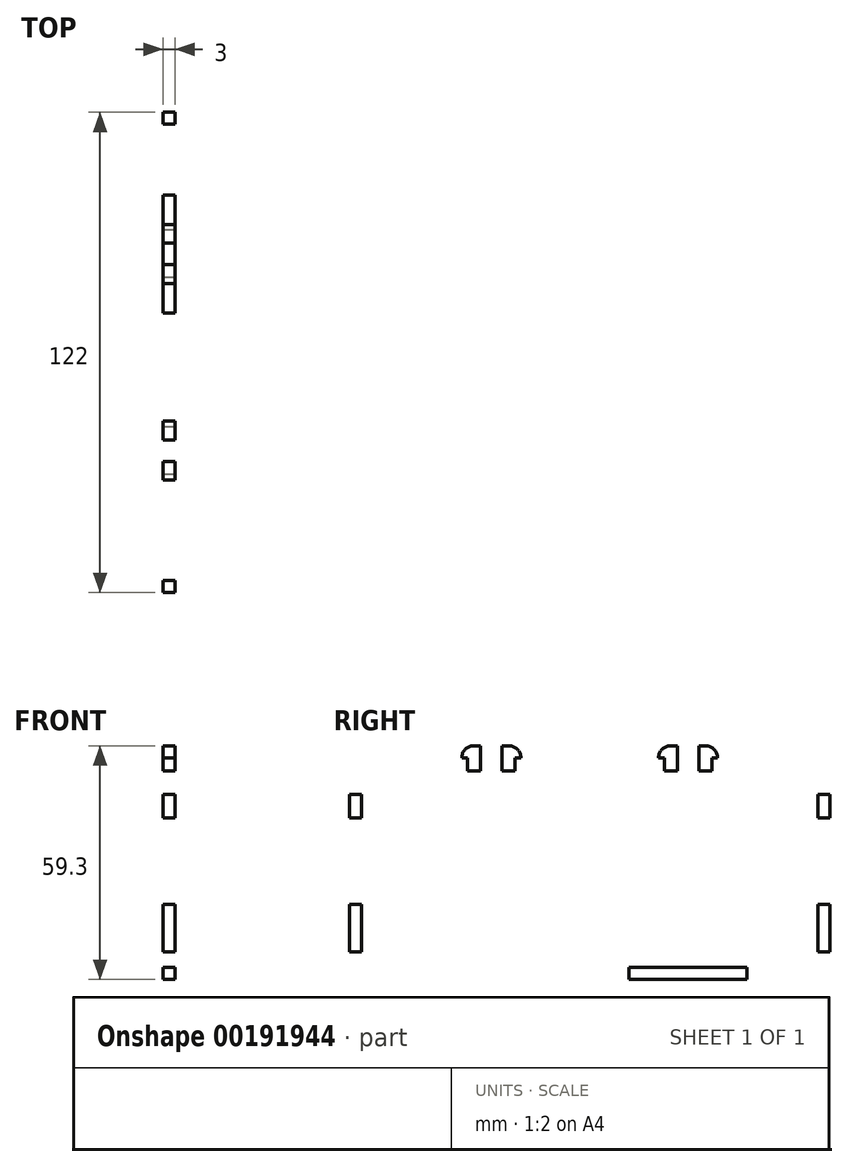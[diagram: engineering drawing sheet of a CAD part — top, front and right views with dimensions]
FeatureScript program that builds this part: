
annotation { "Feature Type Name" : "Feature", "Feature Type Description" : "" }
export const myFeature = defineFeature(function(context is Context, id is Id, definition is map)
    precondition{}
    {
        {
            var Q0;
            Q0=qCreatedBy(makeId("Right.planeOp"),FACE);
            var sketch = newSketch(context, id + "F0", { "sketchPlane" : qUnion([Q0])});
            skLineSegment(sketch, "E0.bottom", {"start": v(58, -25) * mm, "end": v(-58, -25) * mm});
            skLineSegment(sketch, "E0.top", {"start": v(58, 25) * mm, "end": v(-58, 25) * mm});
            skLineSegment(sketch, "E0.left", {"start": v(58, -25) * mm, "end": v(58, 25) * mm});
            skLineSegment(sketch, "E0.right", {"start": v(-58, -25) * mm, "end": v(-58, 25) * mm});
            skPoint(sketch, "E0.middle", {"position": v(0, 0) * mm});
            skLineSegment(sketch, "E1.bottom", {"start": v(-10, -25) * mm, "end": v(-40, -25) * mm});
            skLineSegment(sketch, "E1.top", {"start": v(-10, -28) * mm, "end": v(-40, -28) * mm});
            skLineSegment(sketch, "E1.left", {"start": v(-10, -25) * mm, "end": v(-10, -28) * mm});
            skLineSegment(sketch, "E1.right", {"start": v(-40, -25) * mm, "end": v(-40, -28) * mm});
            skLineSegment(sketch, "E2.bottom", {"start": v(-50.3, -25) * mm, "end": v(-47, -25) * mm});
            skLineSegment(sketch, "E2.top", {"start": v(-50.3, -17) * mm, "end": v(-47, -17) * mm});
            skLineSegment(sketch, "E2.left", {"start": v(-50.3, -25) * mm, "end": v(-50.3, -17) * mm});
            skLineSegment(sketch, "E2.right", {"start": v(-47, -25) * mm, "end": v(-47, -17) * mm});
            skPoint(sketch, "E3", {"position": v(-48.65, -25) * mm});
            skLineSegment(sketch, "E4.bottom", {"start": v(-45.15, -21) * mm, "end": v(-52.15, -21) * mm});
            skLineSegment(sketch, "E4.top", {"start": v(-45.15, -19) * mm, "end": v(-52.15, -19) * mm});
            skLineSegment(sketch, "E4.left", {"start": v(-45.15, -21) * mm, "end": v(-45.15, -19) * mm});
            skLineSegment(sketch, "E4.right", {"start": v(-52.15, -21) * mm, "end": v(-52.15, -19) * mm});
            skPoint(sketch, "E4.middle", {"position": v(-48.65, -20) * mm});
            skCircle(sketch, "E5", {"center": v(-52.15, -21) * mm, "radius": 0.5 * mm});
            skCircle(sketch, "E6", {"center": v(-45.15, -21) * mm, "radius": 0.5 * mm});
            skPoint(sketch, "E7", {"position": v(-58, 0) * mm});
            skLineSegment(sketch, "E8.bottom", {"start": v(-58, -1.65) * mm, "end": v(-50, -1.65) * mm});
            skLineSegment(sketch, "E8.top", {"start": v(-58, 1.65) * mm, "end": v(-50, 1.65) * mm});
            skLineSegment(sketch, "E8.left", {"start": v(-58, -1.65) * mm, "end": v(-58, 1.65) * mm});
            skLineSegment(sketch, "E8.right", {"start": v(-50, -1.65) * mm, "end": v(-50, 1.65) * mm});
            skPoint(sketch, "E8.middle", {"position": v(-54, 0) * mm});
            skLineSegment(sketch, "E9.bottom", {"start": v(-52, -3.5) * mm, "end": v(-54, -3.5) * mm});
            skLineSegment(sketch, "E9.top", {"start": v(-52, 3.5) * mm, "end": v(-54, 3.5) * mm});
            skLineSegment(sketch, "E9.left", {"start": v(-52, -3.5) * mm, "end": v(-52, 3.5) * mm});
            skLineSegment(sketch, "E9.right", {"start": v(-54, -3.5) * mm, "end": v(-54, 3.5) * mm});
            skPoint(sketch, "E9.middle", {"position": v(-53, 0) * mm});
            skCircle(sketch, "E10", {"center": v(-54, 3.5) * mm, "radius": 0.5 * mm});
            skCircle(sketch, "E11", {"center": v(-54, -3.5) * mm, "radius": 0.5 * mm});
            skLineSegment(sketch, "E12.bottom", {"start": v(-58, -21) * mm, "end": v(-61, -21) * mm});
            skLineSegment(sketch, "E12.top", {"start": v(-58, -9) * mm, "end": v(-61, -9) * mm});
            skLineSegment(sketch, "E12.left", {"start": v(-58, -21) * mm, "end": v(-58, -9) * mm});
            skLineSegment(sketch, "E12.right", {"start": v(-61, -21) * mm, "end": v(-61, -9) * mm});
            skLineSegment(sketch, "E13.bottom", {"start": v(-58, 19) * mm, "end": v(-61, 19) * mm});
            skLineSegment(sketch, "E13.top", {"start": v(-58, 13) * mm, "end": v(-61, 13) * mm});
            skLineSegment(sketch, "E13.left", {"start": v(-58, 19) * mm, "end": v(-58, 13) * mm});
            skLineSegment(sketch, "E13.right", {"start": v(-61, 19) * mm, "end": v(-61, 13) * mm});
            skCircle(sketch, "E14.MirrorC", {"center": v(54, -3.5) * mm, "radius": 0.5 * mm});
            skCircle(sketch, "E15.MirrorC", {"center": v(54, 3.5) * mm, "radius": 0.5 * mm});
            skLineSegment(sketch, "E16.MirrorCS", {"start": v(58, 1.65) * mm, "end": v(50, 1.65) * mm});
            skLineSegment(sketch, "E17.MirrorCS", {"start": v(52, -3.5) * mm, "end": v(54, -3.5) * mm});
            skCircle(sketch, "E18.MirrorC", {"center": v(45.15, -21) * mm, "radius": 0.5 * mm});
            skLineSegment(sketch, "E19.MirrorCS", {"start": v(52.15, -21) * mm, "end": v(52.15, -19) * mm});
            skCircle(sketch, "E20.MirrorC", {"center": v(52.15, -21) * mm, "radius": 0.5 * mm});
            skLineSegment(sketch, "E21.MirrorCS", {"start": v(52, 3.5) * mm, "end": v(54, 3.5) * mm});
            skLineSegment(sketch, "E22.MirrorCS", {"start": v(45.15, -19) * mm, "end": v(52.15, -19) * mm});
            skLineSegment(sketch, "E23.MirrorCS", {"start": v(58, -1.65) * mm, "end": v(50, -1.65) * mm});
            skLineSegment(sketch, "E24.MirrorCS", {"start": v(58, 13) * mm, "end": v(61, 13) * mm});
            skLineSegment(sketch, "E25.MirrorCS", {"start": v(50, -1.65) * mm, "end": v(50, 1.65) * mm});
            skLineSegment(sketch, "E26.MirrorCS", {"start": v(52, -3.5) * mm, "end": v(52, 3.5) * mm});
            skLineSegment(sketch, "E27.MirrorCS", {"start": v(58, -21) * mm, "end": v(61, -21) * mm});
            skLineSegment(sketch, "E28.MirrorCS", {"start": v(45.15, -21) * mm, "end": v(45.15, -19) * mm});
            skLineSegment(sketch, "E29.MirrorCS", {"start": v(10, -25) * mm, "end": v(10, -28) * mm});
            skLineSegment(sketch, "E30.MirrorCS", {"start": v(58, 19) * mm, "end": v(61, 19) * mm});
            skLineSegment(sketch, "E31.MirrorCS", {"start": v(47, -25) * mm, "end": v(47, -17) * mm});
            skLineSegment(sketch, "E32.MirrorCS", {"start": v(50.3, -25) * mm, "end": v(47, -25) * mm});
            skLineSegment(sketch, "E33.MirrorCS", {"start": v(40, -25) * mm, "end": v(40, -28) * mm});
            skLineSegment(sketch, "E34.MirrorCS", {"start": v(58, -9) * mm, "end": v(61, -9) * mm});
            skLineSegment(sketch, "E35.MirrorCS", {"start": v(50.3, -25) * mm, "end": v(50.3, -17) * mm});
            skLineSegment(sketch, "E36.MirrorCS", {"start": v(58, -1.65) * mm, "end": v(58, 1.65) * mm});
            skLineSegment(sketch, "E37.MirrorCS", {"start": v(50.3, -17) * mm, "end": v(47, -17) * mm});
            skLineSegment(sketch, "E38.MirrorCS", {"start": v(54, -3.5) * mm, "end": v(54, 3.5) * mm});
            skLineSegment(sketch, "E39.MirrorCS", {"start": v(45.15, -21) * mm, "end": v(52.15, -21) * mm});
            skLineSegment(sketch, "E40.MirrorCS", {"start": v(61, 19) * mm, "end": v(61, 13) * mm});
            skLineSegment(sketch, "E41.MirrorCS", {"start": v(58, 19) * mm, "end": v(58, 13) * mm});
            skLineSegment(sketch, "E42.MirrorCS", {"start": v(61, -21) * mm, "end": v(61, -9) * mm});
            skPoint(sketch, "E43.MirrorP", {"position": v(48.65, -20) * mm});
            skPoint(sketch, "E44.MirrorP", {"position": v(54, 0) * mm});
            skLineSegment(sketch, "E45.MirrorCS", {"start": v(58, -21) * mm, "end": v(58, -9) * mm});
            skLineSegment(sketch, "E46.MirrorCS", {"start": v(10, -28) * mm, "end": v(40, -28) * mm});
            skLineSegment(sketch, "E47.MirrorCS", {"start": v(10, -25) * mm, "end": v(40, -25) * mm});
            skPoint(sketch, "E48.MirrorP", {"position": v(48.65, -25) * mm});
            skPoint(sketch, "E49.MirrorP", {"position": v(53, 0) * mm});
            skPoint(sketch, "E50.MirrorP", {"position": v(58, 0) * mm});
            skPoint(sketch, "E51", {"position": v(-31, 25) * mm});
            skPoint(sketch, "E52", {"position": v(-27.7, 25) * mm});
            skPoint(sketch, "E53", {"position": v(-34, 25) * mm});
            skPoint(sketch, "E54", {"position": v(-34, 15) * mm});
            skPoint(sketch, "E55", {"position": v(-31, 15) * mm});
            skPoint(sketch, "E56", {"position": v(-27.7, 15) * mm});
            skPoint(sketch, "E57", {"position": v(-34.3, 5) * mm});
            skPoint(sketch, "E58", {"position": v(-31, 5) * mm});
            skPoint(sketch, "E59", {"position": v(-37.3, 5) * mm});
            skLineSegment(sketch, "E60", {"start": v(-34, 25) * mm, "end": v(-34, 19.82) * mm});
            skLineSegment(sketch, "E61", {"start": v(-35.51, 10.42) * mm, "end": v(-35.79, 9.58) * mm});
            skLineSegment(sketch, "E62", {"start": v(-31, 25) * mm, "end": v(-31, 19.82) * mm});
            skLineSegment(sketch, "E63", {"start": v(-32.79, 9.58) * mm, "end": v(-32.51, 10.42) * mm});
            skLineSegment(sketch, "E64", {"start": v(-27.7, 25) * mm, "end": v(-27.7, 19.82) * mm});
            skLineSegment(sketch, "E65", {"start": v(-29.49, 9.58) * mm, "end": v(-29.21, 10.42) * mm});
            skPoint(sketch, "E66", {"position": v(-37.3, -5) * mm});
            skPoint(sketch, "E67", {"position": v(-34.3, -5) * mm});
            skPoint(sketch, "E68", {"position": v(-31, -5) * mm});
            skLineSegment(sketch, "E69", {"start": v(-37.3, 0.18) * mm, "end": v(-37.3, -5) * mm});
            skLineSegment(sketch, "E70", {"start": v(-34.3, 0.18) * mm, "end": v(-34.3, -5) * mm});
            skLineSegment(sketch, "E71", {"start": v(-31, 0.18) * mm, "end": v(-31, -5) * mm});
            skArc(sketch, "E72", {"start": v(-37.3, -5) * mm, "mid": v(-35.8, -6.5) * mm, "end": v(-34.3, -5) * mm});
            skArc(sketch, "E73", {"start": v(-31, -5) * mm, "mid": v(-25, -11) * mm, "end": v(-19, -5) * mm});
            skArc(sketch, "E74.filletArc", {"start": v(-35.51, 10.42) * mm, "mid": v(-34.38, 15.06) * mm, "end": v(-34, 19.82) * mm});
            skArc(sketch, "E75.filletArc", {"start": v(-35.79, 9.58) * mm, "mid": v(-36.92, 4.94) * mm, "end": v(-37.3, 0.18) * mm});
            skArc(sketch, "E76.filletArc", {"start": v(-32.51, 10.42) * mm, "mid": v(-31.38, 15.06) * mm, "end": v(-31, 19.82) * mm});
            skArc(sketch, "E77.filletArc", {"start": v(-32.79, 9.58) * mm, "mid": v(-33.92, 4.94) * mm, "end": v(-34.3, 0.18) * mm});
            skArc(sketch, "E78.filletArc", {"start": v(-29.21, 10.42) * mm, "mid": v(-28.08, 15.06) * mm, "end": v(-27.7, 19.82) * mm});
            skArc(sketch, "E79.filletArc", {"start": v(-29.49, 9.58) * mm, "mid": v(-30.62, 4.94) * mm, "end": v(-31, 0.18) * mm});
            skLineSegment(sketch, "E80", {"start": v(-31, 25) * mm, "end": v(-31, 28.3) * mm});
            skLineSegment(sketch, "E81", {"start": v(-31, 28.3) * mm, "end": v(-32.5, 28.3) * mm});
            skLineSegment(sketch, "E82", {"start": v(-32.5, 28.3) * mm, "end": v(-32.5, 28.3) * mm});
            skLineSegment(sketch, "E83", {"start": v(-29.5, 31.3) * mm, "end": v(-27.7, 31.3) * mm});
            skLineSegment(sketch, "E84", {"start": v(-27.7, 31.3) * mm, "end": v(-27.7, 25) * mm});
            skPoint(sketch, "E85.visualSharp", {"position": v(-32.5, 31.3) * mm});
            skArc(sketch, "E85.filletArc", {"start": v(-29.5, 31.3) * mm, "mid": v(-31.62, 30.42) * mm, "end": v(-32.5, 28.3) * mm});
            skPoint(sketch, "E86", {"position": v(-25, 25) * mm});
            skLineSegment(sketch, "E87", {"start": v(-25, 25) * mm, "end": v(-25, -5) * mm});
            skPoint(sketch, "E88.MirrorP", {"position": v(-22.3, 15) * mm});
            skLineSegment(sketch, "E89.MirrorCS", {"start": v(-20.5, 31.3) * mm, "end": v(-22.3, 31.3) * mm});
            skLineSegment(sketch, "E90.MirrorCS", {"start": v(-22.3, 31.3) * mm, "end": v(-22.3, 25) * mm});
            skLineSegment(sketch, "E91.MirrorCS", {"start": v(-22.3, 25) * mm, "end": v(-22.3, 19.82) * mm});
            skArc(sketch, "E92.MirrorCS", {"start": v(-20.79, 10.42) * mm, "mid": v(-21.92, 15.06) * mm, "end": v(-22.3, 19.82) * mm});
            skArc(sketch, "E93.MirrorCS", {"start": v(-12.7, -5) * mm, "mid": v(-14.2, -6.5) * mm, "end": v(-15.7, -5) * mm});
            skLineSegment(sketch, "E94.MirrorCS", {"start": v(-14.49, 10.42) * mm, "end": v(-14.21, 9.58) * mm});
            skLineSegment(sketch, "E95.MirrorCS", {"start": v(-20.51, 9.58) * mm, "end": v(-20.79, 10.42) * mm});
            skLineSegment(sketch, "E96.MirrorCS", {"start": v(-17.21, 9.58) * mm, "end": v(-17.49, 10.42) * mm});
            skLineSegment(sketch, "E97.MirrorCS", {"start": v(-19, 28.3) * mm, "end": v(-17.5, 28.3) * mm});
            skLineSegment(sketch, "E98.MirrorCS", {"start": v(-17.5, 28.3) * mm, "end": v(-17.5, 28.3) * mm});
            skPoint(sketch, "E99.MirrorP", {"position": v(-15.7, 5) * mm});
            skPoint(sketch, "E100.MirrorP", {"position": v(-19, 15) * mm});
            skPoint(sketch, "E101.MirrorP", {"position": v(-19, 5) * mm});
            skPoint(sketch, "E102.MirrorP", {"position": v(-16, 15) * mm});
            skPoint(sketch, "E103.MirrorP", {"position": v(-12.7, 5) * mm});
            skPoint(sketch, "E104.MirrorP", {"position": v(-15.7, -5) * mm});
            skLineSegment(sketch, "E105.MirrorCS", {"start": v(-19, 25) * mm, "end": v(-19, 28.3) * mm});
            skArc(sketch, "E106.MirrorCS", {"start": v(-14.21, 9.58) * mm, "mid": v(-13.08, 4.94) * mm, "end": v(-12.7, 0.18) * mm});
            skArc(sketch, "E107.MirrorCS", {"start": v(-17.21, 9.58) * mm, "mid": v(-16.08, 4.94) * mm, "end": v(-15.7, 0.18) * mm});
            skPoint(sketch, "E108.MirrorP", {"position": v(-12.7, -5) * mm});
            skLineSegment(sketch, "E109.MirrorCS", {"start": v(-15.7, 0.18) * mm, "end": v(-15.7, -5) * mm});
            skArc(sketch, "E110.MirrorCS", {"start": v(-17.49, 10.42) * mm, "mid": v(-18.62, 15.06) * mm, "end": v(-19, 19.82) * mm});
            skLineSegment(sketch, "E111.MirrorCS", {"start": v(-12.7, 0.18) * mm, "end": v(-12.7, -5) * mm});
            skArc(sketch, "E112.MirrorCS", {"start": v(-14.49, 10.42) * mm, "mid": v(-15.62, 15.06) * mm, "end": v(-16, 19.82) * mm});
            skLineSegment(sketch, "E113.MirrorCS", {"start": v(-19, 0.18) * mm, "end": v(-19, -5) * mm});
            skPoint(sketch, "E114.MirrorP", {"position": v(-17.5, 31.3) * mm});
            skPoint(sketch, "E115.MirrorP", {"position": v(-19, -5) * mm});
            skArc(sketch, "E116.MirrorCS", {"start": v(-20.5, 31.3) * mm, "mid": v(-18.38, 30.42) * mm, "end": v(-17.5, 28.3) * mm});
            skLineSegment(sketch, "E117.MirrorCS", {"start": v(-16, 25) * mm, "end": v(-16, 19.82) * mm});
            skLineSegment(sketch, "E118.MirrorCS", {"start": v(-19, 25) * mm, "end": v(-19, 19.82) * mm});
            skArc(sketch, "E119.MirrorCS", {"start": v(-20.51, 9.58) * mm, "mid": v(-19.38, 4.94) * mm, "end": v(-19, 0.18) * mm});
            skPoint(sketch, "E120.MirrorP", {"position": v(-19, 25) * mm});
            skPoint(sketch, "E121.MirrorP", {"position": v(-16, 25) * mm});
            skLineSegment(sketch, "E122.MirrorCS", {"start": v(31, 28.3) * mm, "end": v(32.5, 28.3) * mm});
            skLineSegment(sketch, "E123.MirrorCS", {"start": v(20.5, 31.3) * mm, "end": v(22.3, 31.3) * mm});
            skLineSegment(sketch, "E124.MirrorCS", {"start": v(29.49, 9.58) * mm, "end": v(29.21, 10.42) * mm});
            skLineSegment(sketch, "E125.MirrorCS", {"start": v(14.49, 10.42) * mm, "end": v(14.21, 9.58) * mm});
            skLineSegment(sketch, "E126.MirrorCS", {"start": v(29.5, 31.3) * mm, "end": v(27.7, 31.3) * mm});
            skLineSegment(sketch, "E127.MirrorCS", {"start": v(17.21, 9.58) * mm, "end": v(17.49, 10.42) * mm});
            skLineSegment(sketch, "E128.MirrorCS", {"start": v(19, 28.3) * mm, "end": v(17.5, 28.3) * mm});
            skLineSegment(sketch, "E129.MirrorCS", {"start": v(20.51, 9.58) * mm, "end": v(20.79, 10.42) * mm});
            skLineSegment(sketch, "E130.MirrorCS", {"start": v(35.51, 10.42) * mm, "end": v(35.79, 9.58) * mm});
            skLineSegment(sketch, "E131.MirrorCS", {"start": v(32.79, 9.58) * mm, "end": v(32.51, 10.42) * mm});
            skPoint(sketch, "E132.MirrorP", {"position": v(19, 15) * mm});
            skArc(sketch, "E133.MirrorCS", {"start": v(12.7, -5) * mm, "mid": v(14.2, -6.5) * mm, "end": v(15.7, -5) * mm});
            skPoint(sketch, "E134.MirrorP", {"position": v(31, 5) * mm});
            skPoint(sketch, "E135.MirrorP", {"position": v(15.7, 5) * mm});
            skLineSegment(sketch, "E136.MirrorCS", {"start": v(19, 25) * mm, "end": v(19, 28.3) * mm});
            skPoint(sketch, "E137.MirrorP", {"position": v(31, 15) * mm});
            skPoint(sketch, "E138.MirrorP", {"position": v(12.7, 5) * mm});
            skPoint(sketch, "E139.MirrorP", {"position": v(34, 15) * mm});
            skArc(sketch, "E140.MirrorCS", {"start": v(29.5, 31.3) * mm, "mid": v(31.62, 30.42) * mm, "end": v(32.5, 28.3) * mm});
            skLineSegment(sketch, "E141.MirrorCS", {"start": v(31, 25) * mm, "end": v(31, 28.3) * mm});
            skPoint(sketch, "E142.MirrorP", {"position": v(37.3, 5) * mm});
            skPoint(sketch, "E143.MirrorP", {"position": v(19, 5) * mm});
            skPoint(sketch, "E144.MirrorP", {"position": v(34.3, 5) * mm});
            skArc(sketch, "E145.MirrorCS", {"start": v(20.5, 31.3) * mm, "mid": v(18.38, 30.42) * mm, "end": v(17.5, 28.3) * mm});
            skPoint(sketch, "E146.MirrorP", {"position": v(27.7, 15) * mm});
            skArc(sketch, "E147.MirrorCS", {"start": v(37.3, -5) * mm, "mid": v(35.8, -6.5) * mm, "end": v(34.3, -5) * mm});
            skPoint(sketch, "E148.MirrorP", {"position": v(16, 15) * mm});
            skArc(sketch, "E149.MirrorCS", {"start": v(32.79, 9.58) * mm, "mid": v(33.92, 4.94) * mm, "end": v(34.3, 0.18) * mm});
            skLineSegment(sketch, "E150.MirrorCS", {"start": v(19, 0.18) * mm, "end": v(19, -5) * mm});
            skLineSegment(sketch, "E151.MirrorCS", {"start": v(12.7, 0.18) * mm, "end": v(12.7, -5) * mm});
            skPoint(sketch, "E152.MirrorP", {"position": v(12.7, -5) * mm});
            skLineSegment(sketch, "E153.MirrorCS", {"start": v(16, 25) * mm, "end": v(16, 19.82) * mm});
            skPoint(sketch, "E154.MirrorP", {"position": v(17.5, 31.3) * mm});
            skLineSegment(sketch, "E155.MirrorCS", {"start": v(34, 25) * mm, "end": v(34, 19.82) * mm});
            skPoint(sketch, "E156.MirrorP", {"position": v(27.7, 25) * mm});
            skArc(sketch, "E157.MirrorCS", {"start": v(32.51, 10.42) * mm, "mid": v(31.38, 15.06) * mm, "end": v(31, 19.82) * mm});
            skLineSegment(sketch, "E158.MirrorCS", {"start": v(34.3, 0.18) * mm, "end": v(34.3, -5) * mm});
            skPoint(sketch, "E159.MirrorP", {"position": v(34, 25) * mm});
            skArc(sketch, "E160.MirrorCS", {"start": v(20.51, 9.58) * mm, "mid": v(19.38, 4.94) * mm, "end": v(19, 0.18) * mm});
            skLineSegment(sketch, "E161.MirrorCS", {"start": v(19, 25) * mm, "end": v(19, 19.82) * mm});
            skLineSegment(sketch, "E162.MirrorCS", {"start": v(31, 0.18) * mm, "end": v(31, -5) * mm});
            skPoint(sketch, "E163.MirrorP", {"position": v(19, -5) * mm});
            skArc(sketch, "E164.MirrorCS", {"start": v(29.21, 10.42) * mm, "mid": v(28.08, 15.06) * mm, "end": v(27.7, 19.82) * mm});
            skLineSegment(sketch, "E165.MirrorCS", {"start": v(31, 25) * mm, "end": v(31, 19.82) * mm});
            skPoint(sketch, "E166.MirrorP", {"position": v(37.3, -5) * mm});
            skArc(sketch, "E167.MirrorCS", {"start": v(35.79, 9.58) * mm, "mid": v(36.92, 4.94) * mm, "end": v(37.3, 0.18) * mm});
            skArc(sketch, "E168.MirrorCS", {"start": v(17.49, 10.42) * mm, "mid": v(18.62, 15.06) * mm, "end": v(19, 19.82) * mm});
            skArc(sketch, "E169.MirrorCS", {"start": v(29.49, 9.58) * mm, "mid": v(30.62, 4.94) * mm, "end": v(31, 0.18) * mm});
            skPoint(sketch, "E170.MirrorP", {"position": v(31, -5) * mm});
            skArc(sketch, "E171.MirrorCS", {"start": v(35.51, 10.42) * mm, "mid": v(34.38, 15.06) * mm, "end": v(34, 19.82) * mm});
            skLineSegment(sketch, "E172.MirrorCS", {"start": v(22.3, 31.3) * mm, "end": v(22.3, 25) * mm});
            skArc(sketch, "E173.MirrorCS", {"start": v(14.49, 10.42) * mm, "mid": v(15.62, 15.06) * mm, "end": v(16, 19.82) * mm});
            skArc(sketch, "E174.MirrorCS", {"start": v(17.21, 9.58) * mm, "mid": v(16.08, 4.94) * mm, "end": v(15.7, 0.18) * mm});
            skPoint(sketch, "E175.MirrorP", {"position": v(31, 25) * mm});
            skArc(sketch, "E176.MirrorCS", {"start": v(14.21, 9.58) * mm, "mid": v(13.08, 4.94) * mm, "end": v(12.7, 0.18) * mm});
            skLineSegment(sketch, "E177.MirrorCS", {"start": v(37.3, 0.18) * mm, "end": v(37.3, -5) * mm});
            skPoint(sketch, "E178.MirrorP", {"position": v(22.3, 15) * mm});
            skLineSegment(sketch, "E179.MirrorCS", {"start": v(22.3, 25) * mm, "end": v(22.3, 19.82) * mm});
            skPoint(sketch, "E180.MirrorP", {"position": v(34.3, -5) * mm});
            skArc(sketch, "E181.MirrorCS", {"start": v(31, -5) * mm, "mid": v(25, -11) * mm, "end": v(19, -5) * mm});
            skPoint(sketch, "E182.MirrorP", {"position": v(15.7, -5) * mm});
            skLineSegment(sketch, "E183.MirrorCS", {"start": v(15.7, 0.18) * mm, "end": v(15.7, -5) * mm});
            skLineSegment(sketch, "E184.MirrorCS", {"start": v(27.7, 25) * mm, "end": v(27.7, 19.82) * mm});
            skLineSegment(sketch, "E185.MirrorCS", {"start": v(25, 25) * mm, "end": v(25, -5) * mm});
            skLineSegment(sketch, "E186.MirrorCS", {"start": v(27.7, 31.3) * mm, "end": v(27.7, 25) * mm});
            skPoint(sketch, "E187.MirrorP", {"position": v(32.5, 31.3) * mm});
            skPoint(sketch, "E188.MirrorP", {"position": v(16, 25) * mm});
            skPoint(sketch, "E189.MirrorP", {"position": v(19, 25) * mm});
            skArc(sketch, "E190.MirrorCS", {"start": v(20.79, 10.42) * mm, "mid": v(21.92, 15.06) * mm, "end": v(22.3, 19.82) * mm});
            skPoint(sketch, "E191.MirrorP", {"position": v(25, 25) * mm});
            skSolve(sketch);
        }
        {
            var Q0;
            {var subQ64=sQuery(id+"F0.wireOp",EDGE,"E1.bottom");Q0=makeQuery(id+"F0.imprint","IMPRINT",FACE,{"disambiguationData":[TD([[makeQuery(id+"F0.imprint","IMPRINT",EDGE,{"derivedFrom":subQ64}),-1.0]])]});}
            var Q1;
            Q1=makeQuery(id+"F0.imprint","IMPRINT",FACE,{"disambiguationData":[TD([[makeQuery(id+"F0.imprint","IMPRINT",EDGE,{"derivedFrom":sQuery(id+"F0.wireOp",EDGE,"E13.bottom")}),1.0]])]});
            var Q2;
            Q2=makeQuery(id+"F0.imprint","IMPRINT",FACE,{"disambiguationData":[TD([[makeQuery(id+"F0.imprint","IMPRINT",EDGE,{"derivedFrom":sQuery(id+"F0.wireOp",EDGE,"E12.bottom")}),-1.0]])]});
            var Q3;
            Q3=makeQuery(id+"F0.imprint","IMPRINT",FACE,{"disambiguationData":[TD([[makeQuery(id+"F0.imprint","IMPRINT",EDGE,{"derivedFrom":sQuery(id+"F0.wireOp",EDGE,"E24.MirrorCS")}),1.0]])]});
            var Q4;
            Q4=makeQuery(id+"F0.imprint","IMPRINT",FACE,{"disambiguationData":[TD([[makeQuery(id+"F0.imprint","IMPRINT",EDGE,{"derivedFrom":sQuery(id+"F0.wireOp",EDGE,"E27.MirrorCS")}),1.0]])]});
            var Q5;
            Q5=makeQuery(id+"F0.imprint","IMPRINT",FACE,{"disambiguationData":[TD([[makeQuery(id+"F0.imprint","IMPRINT",EDGE,{"derivedFrom":sQuery(id+"F0.wireOp",EDGE,"E29.MirrorCS")}),1.0]])]});
            var Q6;
            Q6=makeQuery(id+"F0.imprint","IMPRINT",FACE,{"disambiguationData":[TD([[makeQuery(id+"F0.imprint","IMPRINT",EDGE,{"derivedFrom":sQuery(id+"F0.wireOp",EDGE,"E1.bottom")}),1.0]])]});
            var Q7;
            Q7=makeQuery(id+"F0.imprint","IMPRINT",FACE,{"disambiguationData":[TD([[makeQuery(id+"F0.imprint","IMPRINT",EDGE,{"derivedFrom":sQuery(id+"F0.wireOp",EDGE,"E83")}),-1.0]])]});
            var Q8;
            Q8=makeQuery(id+"F0.imprint","IMPRINT",FACE,{"disambiguationData":[TD([[makeQuery(id+"F0.imprint","IMPRINT",EDGE,{"derivedFrom":sQuery(id+"F0.wireOp",EDGE,"4k7hBc77-pQSg-nhAP-8T0Z-smI4ikGxdK0y")}),1.0]])]});
            var Q9;
            {var subQ0=sQuery(id+"F0.wireOp",EDGE,"ec5a9a13-fac2-4802-b096-1cb10d5081ab22.MirrorCS");Q9=makeQuery(id+"F0.imprint","IMPRINT",FACE,{"disambiguationData":[TD([[makeQuery(id+"F0.imprint","IMPRINT",EDGE,{"derivedFrom":subQ0}),-1.0]])]});}
            var Q10;
            {var subQ5=sQuery(id+"F0.wireOp",EDGE,"ec5a9a13-fac2-4802-b096-1cb10d5081ab18.MirrorCS");Q10=makeQuery(id+"F0.imprint","IMPRINT",FACE,{"disambiguationData":[TD([[makeQuery(id+"F0.imprint","IMPRINT",EDGE,{"derivedFrom":subQ5}),-1.0]])]});}
            var Q11;
            {var subQ1=sQuery(id+"F0.wireOp",EDGE,"7b7d0c0d-a1a2-4250-80d7-31fc4aaa65650.MirrorCS");Q11=makeQuery(id+"F0.imprint","IMPRINT",FACE,{"disambiguationData":[TD([[makeQuery(id+"F0.imprint","IMPRINT",EDGE,{"derivedFrom":subQ1}),-1.0]])]});}
            var Q12;
            {var subQ1=sQuery(id+"F0.wireOp",EDGE,"7b7d0c0d-a1a2-4250-80d7-31fc4aaa65652.MirrorCS");Q12=makeQuery(id+"F0.imprint","IMPRINT",FACE,{"disambiguationData":[TD([[makeQuery(id+"F0.imprint","IMPRINT",EDGE,{"derivedFrom":subQ1}),1.0]])]});}
            var Q13;
            Q13=makeQuery(id+"F0.imprint","IMPRINT",FACE,{"disambiguationData":[TD([[makeQuery(id+"F0.imprint","IMPRINT",EDGE,{"derivedFrom":sQuery(id+"F0.wireOp",EDGE,"E89.MirrorCS")}),1.0]])]});
            var Q14;
            Q14=makeQuery(id+"F0.imprint","IMPRINT",FACE,{"disambiguationData":[TD([[makeQuery(id+"F0.imprint","IMPRINT",EDGE,{"derivedFrom":sQuery(id+"F0.wireOp",EDGE,"E123.MirrorCS")}),-1.0]])]});
            var Q15;
            Q15=makeQuery(id+"F0.imprint","IMPRINT",FACE,{"disambiguationData":[TD([[makeQuery(id+"F0.imprint","IMPRINT",EDGE,{"derivedFrom":sQuery(id+"F0.wireOp",EDGE,"E122.MirrorCS")}),1.0]])]});
            extrude(context, id + "F1", {"entities" : qUnion([Q0, Q1, Q2, Q3, Q4, Q5, Q6, Q7, Q8, Q9, Q10, Q11, Q12, Q13, Q14, Q15]), "depth" : 3 * mm, "symmetric" : true});
        }
    });
